# Revit family: 0067964 Sylvania Lighting Fixture START Waterproof Twin 1200 IP65 4800lm 865
name_source: partatom
category: Lighting Fixtures
revit_build: Autodesk Revit 2016 (Build: 20150220_1215(x64)
units: mm (PartAtom-declared; Revit-internal decimal feet)

## family parameters
Cut with Voids When Loaded = No
Host = Face
Light Source = Yes
OmniClass Number = 23.80.70.11.14
OmniClass Title = General Luminaries, Directional
Part Type = Normal
Room Calculation Point = No
Round Connector Dimension = Use Diameter
Shared = No

## types (1)
- 0067964 ST WTRPRF T 1200 IP65 4800LM 865
    AccessoryMaterial = Diffuser-Sylvania-Glow
    Apparent Load = 38 VA
    Assembly Code = D5020200
    AssetType = Fixed
    BodyMaterial = Body-Sylvania-Gray
    ClassificationName = Uniclass2015
    ClassificationValue = EF_70_80
    Color Filter = 16777215
    Cost = 0 $
    Default Elevation = 1219 mm
    Description = Start Waterproof, integrated LED weatherproof luminaire, with UV stabilized flat diffuser and linear prisms designed to achieve uniform lit appearance, optimise light output and to reduce glare, stainless steel diffuser clips and fixing brackets for surface mounting. Polycarbonate housing, Polycarbonate diffuser, 4800lm, 38W, 127lm/W, 6500K, drive current 350mA, non dimmable, CRI80, IP65, IK08, Class I, nominal average lifetime (h): 50000, 1278mm x 110mm x 78mm, energy class: A++ A+ A
    DiffuserMaterial = Diffuser-Sylvania-Transparent
    Dimming Lamp Color Temperature Shift = <None>
    DocumentationLiterature = http://www.sylvania-lighting.com
    DurationUnit = hours
    ElectricShockClassification = Class I
    Emit Shape Visible in Rendering = No
    Emit from Rectangle Length = 1252 mm  [stored 4.10761 ft]
    Emit from Rectangle Width = 90 mm  [stored 0.295276 ft]
    ExpectedLife = 50000
    IfcExportAs = IfcLightFixtureType
    IfcExportType = IfcLightFixtureType
    ImpactProtectionIndex = IK08
    IngressProtection = IP65
    Keynote = 16500
    Lamp = LED
    LampColourRenderingIndex = 80
    LampColourTemperature = 6500 K
    LampNominalLuminous = 4800 lm
    LampsType = LED
    Length = 1272 mm  [stored 4.17323 ft]
    LuminousEfficacy = 127 lm/W
    Manufacturer = Feilo Sylvania
    ManufacturerName = Feilo Sylvania
    Material = polycarbonate housing, polycarbonate diffuser
    Model = START Waterproof Twin 1200 IP65 4800lm 865
    ModelNumber = 0067964
    ModelReference = START Waterproof Twin 1200 IP65 4800lm 865
    Name = START Waterproof Twin 1200 IP65 4800lm 865
    NominalHeight = 78 mm  [stored 0.255906 ft]
    NominalLength = 1278 mm  [stored 4.19291 ft]
    NominalWidth = 0 mm  [stored 0 ft]
    Photometric Web File = 0067964.ies
    PowerConsumption = 38 W
    PowerFactor = 0
    ReflectorMaterial = <By Category>
    Tilt Angle = -90.00°
    Type Image = <None>
    TypeName = START Waterproof Twin 1200 IP65 4800lm 865
    URL = http://www.sylvania-lighting.com
    Voltage = 0 V
    Weight = 1.82 kg
    Width = 110 mm  [stored 0.360892 ft]

note: [stored X ft] marks values corroborated as IEEE doubles in the binary element streams (Revit-internal decimal feet)

## geometry (parser evidence)
native form markers: Sweep x3
no freeform markers — native parametric forms only
